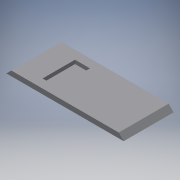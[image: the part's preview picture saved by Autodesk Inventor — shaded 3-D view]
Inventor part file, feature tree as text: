
AUTODESK INVENTOR PART (.ipt)
format: ipt  version: 2018.3 (Build 223284000, 284)  size: 257,024 bytes
history: native  units: mm
features: extrude x4, sketch x4, chamfer x2
ambient origin geometry x8: Origin, YZ Plane, XZ Plane, XY Plane, X Axis, Y Axis, Z Axis, Center Point
bodies: Solid1 (feature_tree)
feature tree (10):
  extrude  "Extrusion1"  Depth=20.0mm
  extrude  "Extrusion2"  Depth=2.0mm
  extrude  "Extrusion3"  Depth=20.0mm TaperAngle=0.0deg
  extrude  "Extrusion4"  Depth=13.0mm
  chamfer  "Chamfer5"  Distance=3.5mm
  chamfer  "Chamfer6"  Distance=3.5mm
  sketch  "Sketch1"  dims[d0=43.0mm d1=20.0mm]
  sketch  "Sketch2"  dims[d2=2.0mm d3=0.0mm d4=2.0mm]
  sketch  "Sketch3"  dims[d5=2.0mm d6=20.0mm d7=0.0mm]
  sketch  "Sketch4"  dims[d8=25.0mm d9=13.0mm d10=3.5mm d11=3.5mm d12=9.0mm d13=9.0mm d14=1.5mm d15=0.0mm d16=19.0mm d17=4.5mm d18=4.5mm d19=1.49mm d20=0.0mm d33=4.5mm d34=1.49mm d35=45.0deg d36=4.5mm d37=1.49mm d38=45.0deg]
